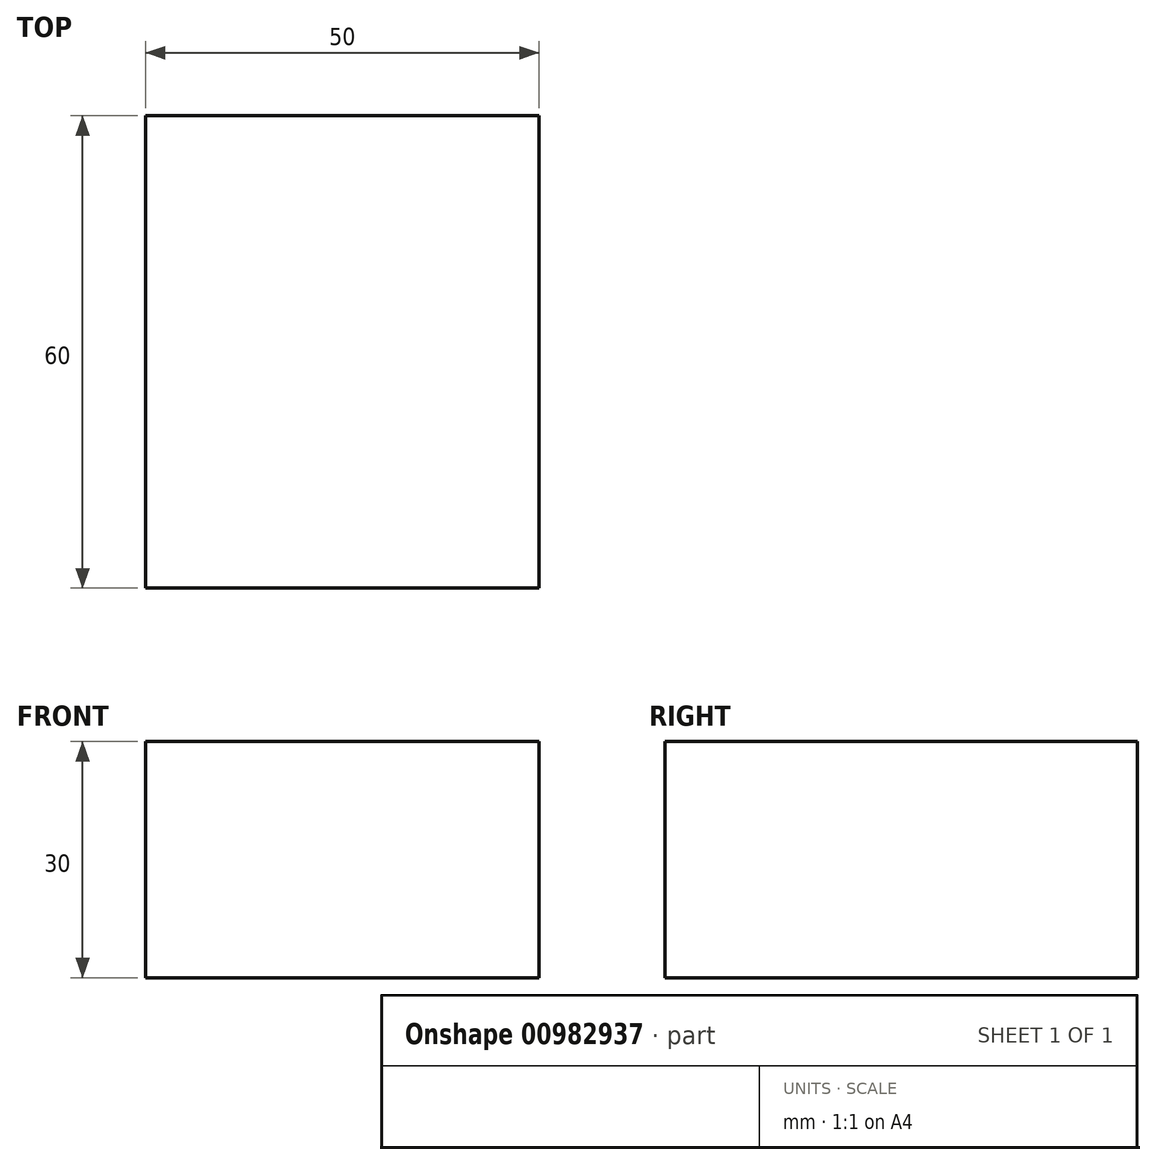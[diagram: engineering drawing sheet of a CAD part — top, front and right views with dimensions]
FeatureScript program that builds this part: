
annotation { "Feature Type Name" : "Feature", "Feature Type Description" : "" }
export const myFeature = defineFeature(function(context is Context, id is Id, definition is map)
    precondition{}
    {
        {
            var Q0;
            Q0=qCreatedBy(makeId("Front.planeOp"),FACE);
            var sketch = newSketch(context, id + "F0", { "sketchPlane" : qUnion([Q0])});
            skLineSegment(sketch, "E0.bottom", {"start": v(25, 15) * mm, "end": v(-25, 15) * mm});
            skLineSegment(sketch, "E0.top", {"start": v(25, -15) * mm, "end": v(-25, -15) * mm});
            skLineSegment(sketch, "E0.left", {"start": v(25, 15) * mm, "end": v(25, -15) * mm});
            skLineSegment(sketch, "E0.right", {"start": v(-25, 15) * mm, "end": v(-25, -15) * mm});
            skPoint(sketch, "E0.middle", {"position": v(0, 0) * mm});
            skSolve(sketch);
        }
        {
            var Q0;
            Q0 = qSketchRegion(id + "F0", true);
            extrude(context, id + "F1", {"entities" : qUnion([Q0]), "depth" : 60 * mm, "offsetDistance" : 25 * mm});
        }
    });
